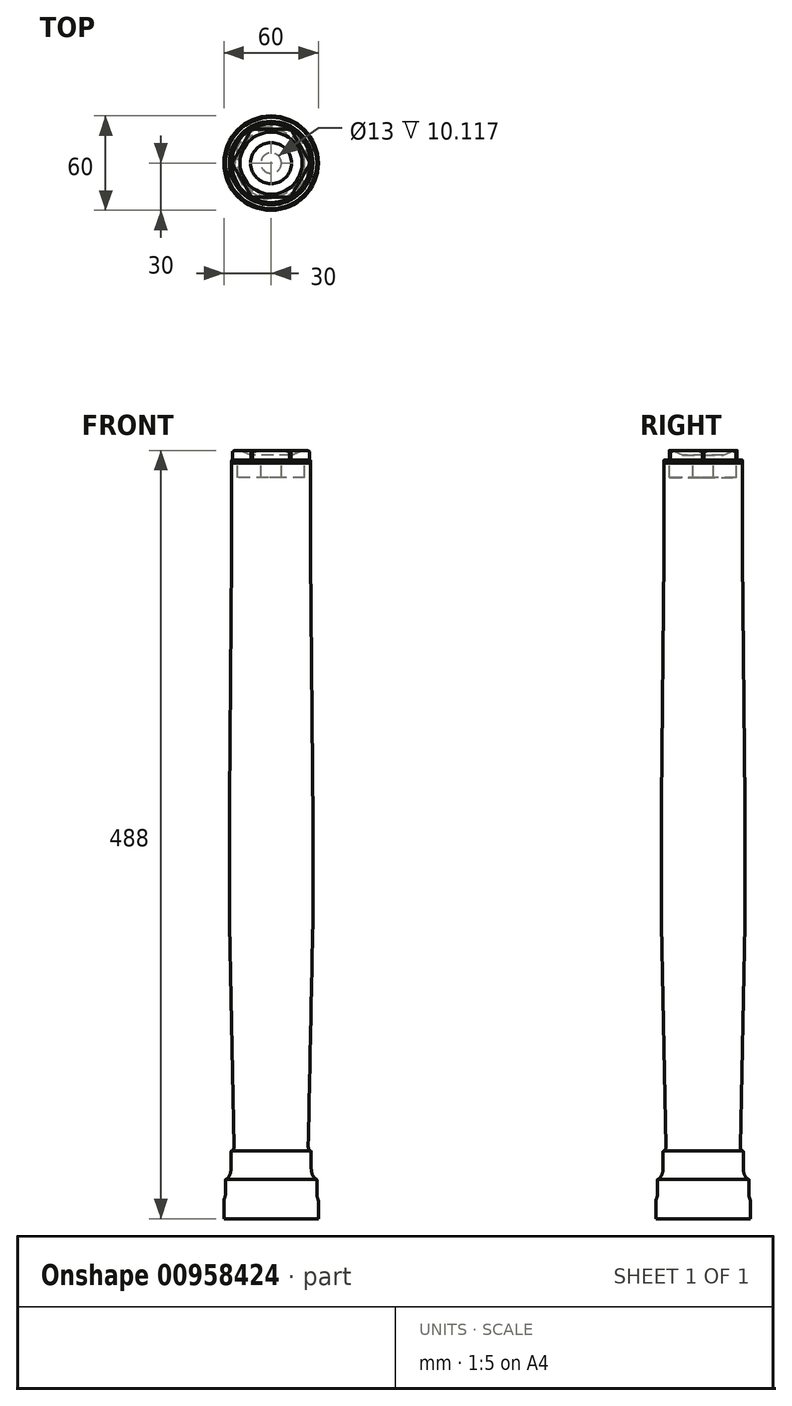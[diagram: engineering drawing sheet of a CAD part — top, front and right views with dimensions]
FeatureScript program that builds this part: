
annotation { "Feature Type Name" : "Feature", "Feature Type Description" : "" }
export const myFeature = defineFeature(function(context is Context, id is Id, definition is map)
    precondition{}
    {
        {
            var Q0;
            Q0=qCreatedBy(makeId("Front.planeOp"),FACE);
            var sketch = newSketch(context, id + "F0", { "sketchPlane" : qUnion([Q0])});
            skLineSegment(sketch, "E0", {"start": v(-25, 30) * mm, "end": v(0, 30) * mm});
            skLineSegment(sketch, "E1", {"start": v(0, 0) * mm, "end": v(0, 475.16) * mm, "construction": true});
            skLineSegment(sketch, "E2", {"start": v(-25, -30) * mm, "end": v(-26.5, -184.98) * mm});
            skLineSegment(sketch, "E3", {"start": v(-26.5, -185.02) * mm, "end": v(-26.5, -262.95) * mm});
            skLineSegment(sketch, "E4", {"start": v(-26.5, -263.05) * mm, "end": v(-23.56, -403.98) * mm});
            skLineSegment(sketch, "E5", {"start": v(-24.77, -407) * mm, "end": v(-25, -407) * mm});
            skLineSegment(sketch, "E6", {"start": v(-25.5, -407.5) * mm, "end": v(-25.5, -418.52) * mm});
            skLineSegment(sketch, "E7", {"start": v(-28.35, -425) * mm, "end": v(-28.75, -425) * mm});
            skLineSegment(sketch, "E8", {"start": v(-29, -425.25) * mm, "end": v(-29, -434.13) * mm});
            skLineSegment(sketch, "E9", {"start": v(-30, -438) * mm, "end": v(-30, -438) * mm});
            skLineSegment(sketch, "E10", {"start": v(-30, -439.13) * mm, "end": v(-30, -450) * mm});
            skLineSegment(sketch, "E11", {"start": v(-30, -450) * mm, "end": v(0, -450) * mm});
            skLineSegment(sketch, "E12", {"start": v(0, 30) * mm, "end": v(0, -450) * mm});
            skPoint(sketch, "E13.visualSharp", {"position": v(-26.5, -185) * mm});
            skArc(sketch, "E13.filletArc", {"start": v(-26.5, -184.98) * mm, "mid": v(-26.5, -185) * mm, "end": v(-26.5, -185.02) * mm});
            skPoint(sketch, "E14.visualSharp", {"position": v(-26.5, -263) * mm});
            skArc(sketch, "E14.filletArc", {"start": v(-26.5, -262.95) * mm, "mid": v(-26.5, -263) * mm, "end": v(-26.5, -263.05) * mm});
            skPoint(sketch, "E15.visualSharp", {"position": v(-23.5, -407) * mm});
            skArc(sketch, "E15.filletArc", {"start": v(-24.34, -406.77) * mm, "mid": v(-23.75, -405.43) * mm, "end": v(-23.56, -403.98) * mm});
            skPoint(sketch, "E16.visualSharp", {"position": v(-24.5, -407) * mm});
            skArc(sketch, "E16.filletArc", {"start": v(-24.77, -407) * mm, "mid": v(-24.52, -406.94) * mm, "end": v(-24.34, -406.77) * mm});
            skPoint(sketch, "E17.visualSharp", {"position": v(-25.5, -407) * mm});
            skArc(sketch, "E17.filletArc", {"start": v(-25, -407) * mm, "mid": v(-25.35, -407.15) * mm, "end": v(-25.5, -407.5) * mm});
            skPoint(sketch, "E18.visualSharp", {"position": v(-25.5, -425) * mm});
            skArc(sketch, "E18.filletArc", {"start": v(-28.18, -424.93) * mm, "mid": v(-26.2, -422) * mm, "end": v(-25.5, -418.52) * mm});
            skPoint(sketch, "E19.visualSharp", {"position": v(-28.25, -425) * mm});
            skArc(sketch, "E19.filletArc", {"start": v(-28.35, -425) * mm, "mid": v(-28.26, -424.98) * mm, "end": v(-28.18, -424.93) * mm});
            skPoint(sketch, "E20.visualSharp", {"position": v(-29, -425) * mm});
            skArc(sketch, "E20.filletArc", {"start": v(-28.75, -425) * mm, "mid": v(-28.93, -425.07) * mm, "end": v(-29, -425.25) * mm});
            skPoint(sketch, "E21.visualSharp", {"position": v(-29, -438) * mm});
            skArc(sketch, "E21.filletArc", {"start": v(-29.62, -437.2) * mm, "mid": v(-29.16, -435.7) * mm, "end": v(-29, -434.13) * mm});
            skPoint(sketch, "E22.visualSharp", {"position": v(-30, -438) * mm});
            skArc(sketch, "E22.filletArc", {"start": v(-29.62, -437.2) * mm, "mid": v(-29.9, -438.15) * mm, "end": v(-30, -439.13) * mm});
            skLineSegment(sketch, "E23", {"start": v(-25, 30) * mm, "end": v(-25, -30) * mm});
            skSolve(sketch);
        }
        {
            var Q0;
            Q0=makeQuery(id+"F0.imprint","IMPRINT",FACE,{"disambiguationData":[TD([[makeQuery(id+"F0.imprint","IMPRINT",EDGE,{"derivedFrom":sQuery(id+"F0.wireOp",EDGE,"E0")}),-1.0]])]});
            var Q1;
            Q1=sQuery(id+"F0.wireOp",EDGE,"E12");
            revolve(context, id + "F1", {"surfaceOperationType" : NewSurfaceOperationType.NEW, "entities" : qUnion([Q0]), "axis" : qUnion([Q1]), "revolveType" : RevolveType.FULL});
        }
        {
            var Q0;
            Q0=qCreatedBy(makeId("Front.planeOp"),FACE);
            var sketch = newSketch(context, id + "F2", { "sketchPlane" : qUnion([Q0])});
            skLineSegment(sketch, "E24", {"start": v(21.29, 20.82) * mm, "end": v(21.29, 30) * mm});
            skLineSegment(sketch, "E25", {"start": v(21.29, 30) * mm, "end": v(25, 30) * mm});
            skLineSegment(sketch, "E26", {"start": v(25, 30) * mm, "end": v(25, 31.5) * mm});
            skLineSegment(sketch, "E27", {"start": v(24.5, 32) * mm, "end": v(24.5, 32) * mm});
            skLineSegment(sketch, "E28", {"start": v(24.5, 32) * mm, "end": v(24.5, 37.28) * mm});
            skLineSegment(sketch, "E29", {"start": v(21.65, 38) * mm, "end": v(19.7, 38) * mm});
            skLineSegment(sketch, "E30", {"start": v(19.7, 38) * mm, "end": v(13, 35) * mm});
            skLineSegment(sketch, "E31", {"start": v(13, 35) * mm, "end": v(0, 35) * mm});
            skLineSegment(sketch, "E32", {"start": v(0, 47.9) * mm, "end": v(0, 19.8) * mm, "construction": true});
            skPoint(sketch, "E33.visualSharp", {"position": v(25, 32) * mm});
            skArc(sketch, "E33.filletArc", {"start": v(25, 31.5) * mm, "mid": v(24.85, 31.85) * mm, "end": v(24.5, 32) * mm});
            skLineSegment(sketch, "E34", {"start": v(21.29, 20.82) * mm, "end": v(6.5, 20.82) * mm});
            skPoint(sketch, "E34.endSnap0", {"position": v(6.5, 35) * mm});
            skLineSegment(sketch, "E35", {"start": v(6.5, 20.82) * mm, "end": v(6.5, 30.93) * mm});
            skLineSegment(sketch, "E36", {"start": v(6.5, 30.93) * mm, "end": v(0, 30.93) * mm});
            skLineSegment(sketch, "E37", {"start": v(0, 30.93) * mm, "end": v(0, 35) * mm});
            skPoint(sketch, "E38.visualSharp", {"position": v(24.5, 38) * mm});
            skArc(sketch, "E38.filletArc", {"start": v(24.5, 37.28) * mm, "mid": v(23.12, 37.82) * mm, "end": v(21.65, 38) * mm});
            skSolve(sketch);
        }
        {
            var Q0;
            Q0=makeQuery(id+"F2.imprint","IMPRINT",FACE,{"disambiguationData":[TD([[makeQuery(id+"F2.imprint","IMPRINT",EDGE,{"derivedFrom":sQuery(id+"F2.wireOp",EDGE,"E24")}),1.0]])]});
            var Q1;
            Q1=sQuery(id+"F2.wireOp",EDGE,"E30");
            var Q2;
            Q2=sQuery(id+"F2.wireOp",EDGE,"E31");
            var Q3;
            Q3=sQuery(id+"F2.wireOp",EDGE,"E32");
            revolve(context, id + "F3", {"surfaceOperationType" : NewSurfaceOperationType.NEW, "entities" : qUnion([Q0]), "surfaceEntities" : qUnion([Q1, Q2]), "axis" : qUnion([Q3]), "revolveType" : RevolveType.FULL});
        }
        {
            var Q0;
            Q0=qCreatedBy(makeId("Top.planeOp"),FACE);
            cPlane(context, id + "F4", {"entities" : qUnion([Q0]), "cplaneType" : CPlaneType.OFFSET, "offset" : 38 * mm, "width" : 150 * mm, "height" : 150 * mm});
        }
        {
            var Q0;
            Q0=qCreatedBy(id+"F4.planeOp",FACE);
            var sketch = newSketch(context, id + "F5", { "sketchPlane" : qUnion([Q0])});
            skCircle(sketch, "E39.cCircle", {"center": v(0, 0) * mm, "radius": 24.83 * mm, "construction": true});
            skLineSegment(sketch, "E39.0", {"start": v(-12.41, 21.5) * mm, "end": v(12.41, 21.5) * mm});
            skLineSegment(sketch, "E39.1", {"start": v(12.41, 21.5) * mm, "end": v(24.83, 0) * mm});
            skLineSegment(sketch, "E39.2", {"start": v(24.83, 0) * mm, "end": v(12.41, -21.5) * mm});
            skLineSegment(sketch, "E39.3", {"start": v(12.41, -21.5) * mm, "end": v(-12.41, -21.5) * mm});
            skLineSegment(sketch, "E39.4", {"start": v(-12.41, -21.5) * mm, "end": v(-24.83, 0) * mm});
            skLineSegment(sketch, "E39.5", {"start": v(-24.83, 0) * mm, "end": v(-12.41, 21.5) * mm});
            skCircle(sketch, "E40", {"center": v(0, 0) * mm, "radius": 29.12 * mm});
            skSolve(sketch);
        }
        {
            var Q0;
            Q0=makeQuery(id+"F5.imprint","IMPRINT",FACE,{"disambiguationData":[TD([[makeQuery(id+"F5.imprint","IMPRINT",EDGE,{"derivedFrom":sQuery(id+"F5.wireOp",EDGE,"E39.0")}),1.0]])]});
            extrude(context, id + "F6", {"entities" : qUnion([Q0]), "operationType" : NewBodyOperationType.REMOVE, "oppositeDirection" : true, "depth" : 6 * mm, "offsetDistance" : 25 * mm});
        }
    });
